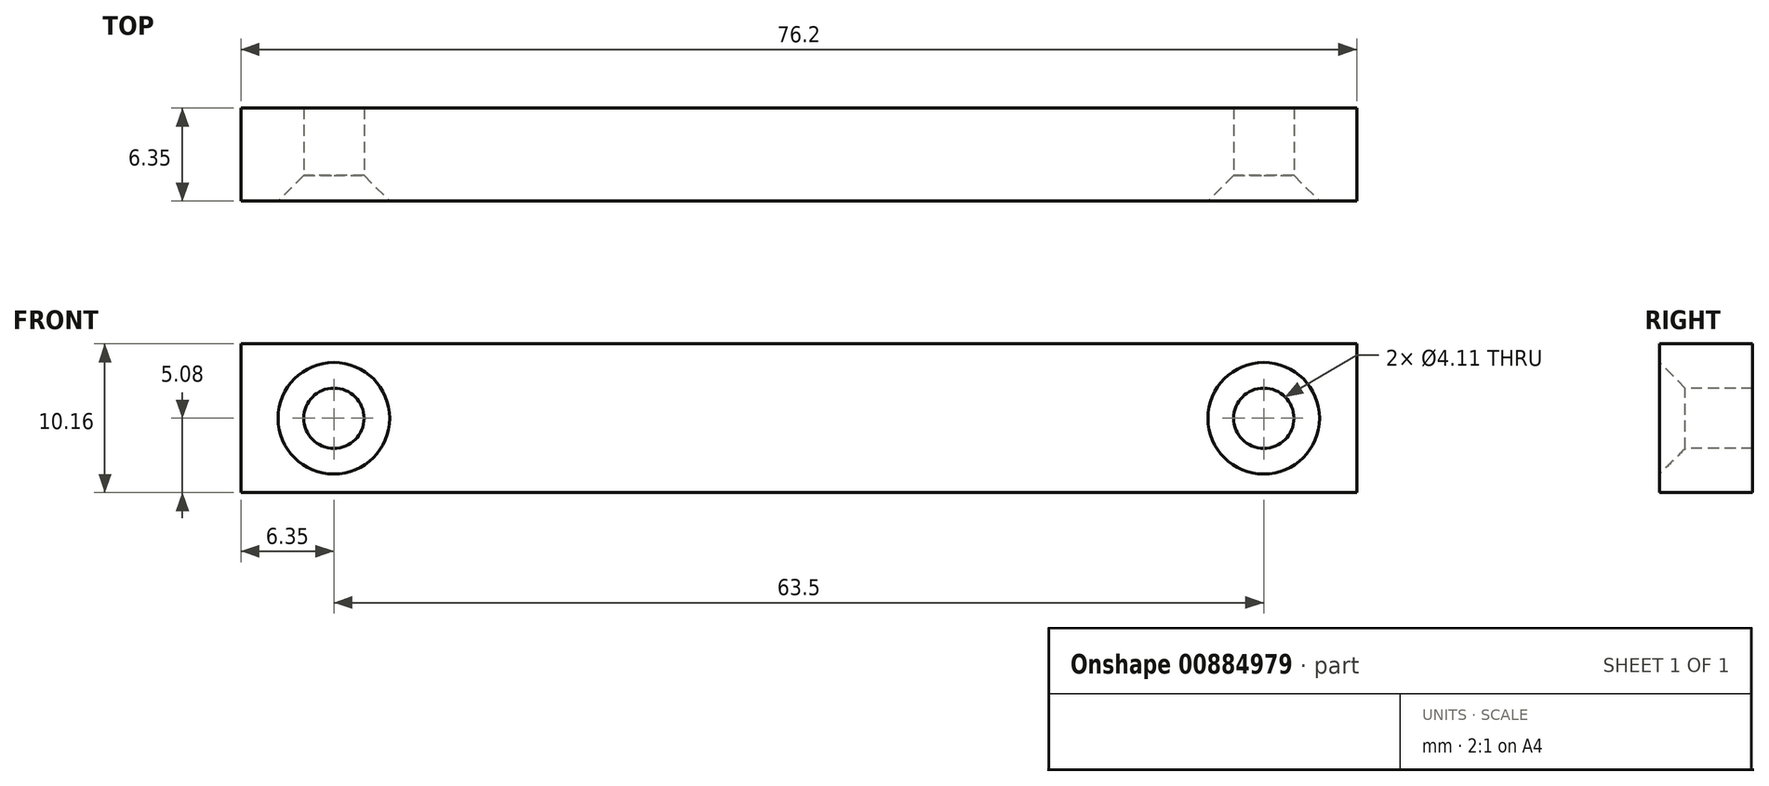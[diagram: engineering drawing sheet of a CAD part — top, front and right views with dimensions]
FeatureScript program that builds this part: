
annotation { "Feature Type Name" : "Feature", "Feature Type Description" : "" }
export const myFeature = defineFeature(function(context is Context, id is Id, definition is map)
    precondition{}
    {
        {
            var Q0;
            Q0=qCreatedBy(makeId("Front.planeOp"),FACE);
            var sketch = newSketch(context, id + "F0", { "sketchPlane" : qUnion([Q0])});
            skLineSegment(sketch, "E0.bottom", {"start": v(0, 0) * mm, "end": v(76.2, 0) * mm});
            skLineSegment(sketch, "E0.top", {"start": v(0, -10.16) * mm, "end": v(76.2, -10.16) * mm});
            skLineSegment(sketch, "E0.left", {"start": v(0, 0) * mm, "end": v(0, -10.16) * mm});
            skLineSegment(sketch, "E0.right", {"start": v(76.2, 0) * mm, "end": v(76.2, -10.16) * mm});
            skSolve(sketch);
        }
        {
            var Q0;
            Q0=makeQuery(id+"F0.imprint","IMPRINT",FACE,{"disambiguationData":[TD([[makeQuery(id+"F0.imprint","IMPRINT",EDGE,{"derivedFrom":sQuery(id+"F0.wireOp",EDGE,"E0.bottom")}),-1.0]])]});
            extrude(context, id + "F1", {"entities" : qUnion([Q0]), "depth" : 6.35 * mm, "offsetDistance" : 25.4 * mm});
        }
        {
            var Q0;
            Q0=makeQuery(id+"F1.opExtrude","CAP_FACE",FACE,{"disambiguationData":[OSD([sQuery(id+"F0.wireOp",EDGE,"E0.bottom"),sQuery(id+"F0.wireOp",EDGE,"E0.top"),sQuery(id+"F0.wireOp",EDGE,"E0.left"),sQuery(id+"F0.wireOp",EDGE,"E0.right")])],"isStart":false});
            var sketch = newSketch(context, id + "F2", { "sketchPlane" : qUnion([Q0])});
            skCircle(sketch, "E1", {"center": v(6.35, -5.08) * mm, "radius": 2.03 * mm});
            skPoint(sketch, "E1.centerSnap0", {"position": v(0, -5.08) * mm});
            skCircle(sketch, "E2", {"center": v(69.85, -5.08) * mm, "radius": 2.03 * mm});
            skPoint(sketch, "E2.centerSnap0", {"position": v(76.2, -5.08) * mm});
            skSolve(sketch);
        }
        {
            var Q0;
            Q0=sQuery(id+"F2.wireOp",VERTEX,"E1.center");
            var Q1;
            Q1=sQuery(id+"F2.wireOp",VERTEX,"E2.center");
            var Q2;
            Q2=makeQuery(id+"F1.opExtrude","SWEPT_BODY",BODY,{"disambiguationData":[OSD([sQuery(id+"F0.wireOp",EDGE,"E0.bottom"),sQuery(id+"F0.wireOp",EDGE,"E0.top"),sQuery(id+"F0.wireOp",EDGE,"E0.left"),sQuery(id+"F0.wireOp",EDGE,"E0.right")])]});
            hole(context, id + "F3", {"style" : HoleStyle.C_SINK, "endStyle" : HoleEndStyle.THROUGH, "holeDiameter" : 4.11 * mm, "cSinkDiameter" : 7.62 * mm, "cSinkAngle" : 90 * degree, "majorDiameter" : 6.35 * mm, "isTappedThrough" : true, "tappedDepth" : 12.7 * mm, "tapClearance" : 3, "locations" : qUnion([Q0, Q1]), "scope" : qUnion([Q2])});
        }
    });
